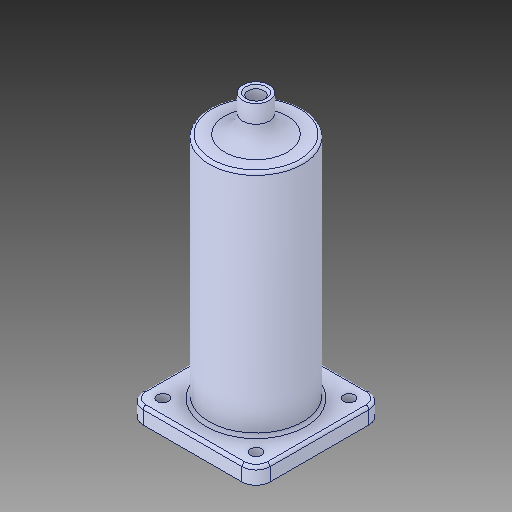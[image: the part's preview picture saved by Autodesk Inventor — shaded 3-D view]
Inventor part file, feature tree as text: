
AUTODESK INVENTOR PART (.ipt)
format: ipt  version: 2018 (Build 220112000, 112)  size: 261,120 bytes
history: native  units: in
note: dims shown in document units (in); Inventor stores cm internally (conversion verified against a paired STEP export)
features: extrude x8, sketch x7, projected_geometry x5, fillet x3, revolve x1, chamfer x1, other x1
ambient origin geometry x8: Origin, YZ Plane, XZ Plane, XY Plane, X Axis, Y Axis, Z Axis, Center Point
bodies: Solid1 (feature_tree)
feature tree (26):
  extrude  "Extrusion1"  TaperAngle=0.0deg  [1 undecoded]
  sketch  "Sketch2"  dims[d4=0.3937in d5=0.0in d6=1.0in d7=0.0in]
  extrude  "Extrusion2"  Depth=1.0in TaperAngle=0.0deg
  extrude  "Extrusion3"  Depth=0.9252in
  sketch  "Sketch3"  dims[d8=2.0in d9=0.0in d10=0.9252in]
  extrude  "Extrusion4"  Depth=2.0in TaperAngle=0.0deg
  extrude  "Extrusion5"  Depth=1.0in
  extrude  "Extrusion6"  Depth=1.0in TaperAngle=0.0deg
  fillet  "Fillet2"  Radius=0.125in
  fillet  "Fillet3"  Radius=1.374in
  extrude  "Extrusion7"  Depth=0.0625in TaperAngle=45.0deg
  extrude  "Extrusion8"  [1 undecoded]
  revolve  "Revolution1"  [1 undecoded]
  chamfer  "Chamfer1"  [1 undecoded]
  fillet  "Fillet1"  [1 undecoded]
  sketch  "Sketch1"  dims[d0=0.0in d1=0.0in d2=0.0in d3=0.0in]
  projected_geometry  "Projected Loop1"
  projected_geometry  "Projected Loop2"
  projected_geometry  "Projected Loop3"
  sketch  "Sketch4"  dims[d11=0.45in d12=2.0in d13=0.0in]
  sketch  "Sketch5"  dims[d14=0.5in d15=1.0in]
  projected_geometry  "Projected Loop4"
  sketch  "Sketch6"  dims[d16=0.25in d17=0.0in d18=1.0in d19=0.0in d20=0.125in d21=1.374in]
  projected_geometry  "Projected Loop5"
  sketch  "Sketch7"  dims[d22=90.0deg d23=0.0625in d24=0.0787in d25=45.0deg]
  other  "Ø8.0mm Dowel Hole1"
note: 5 required parameter values undecoded (feature->parameter linkage not recoverable at this tier; creation-order binding heuristic only, values carry confidence <= 0.55)
